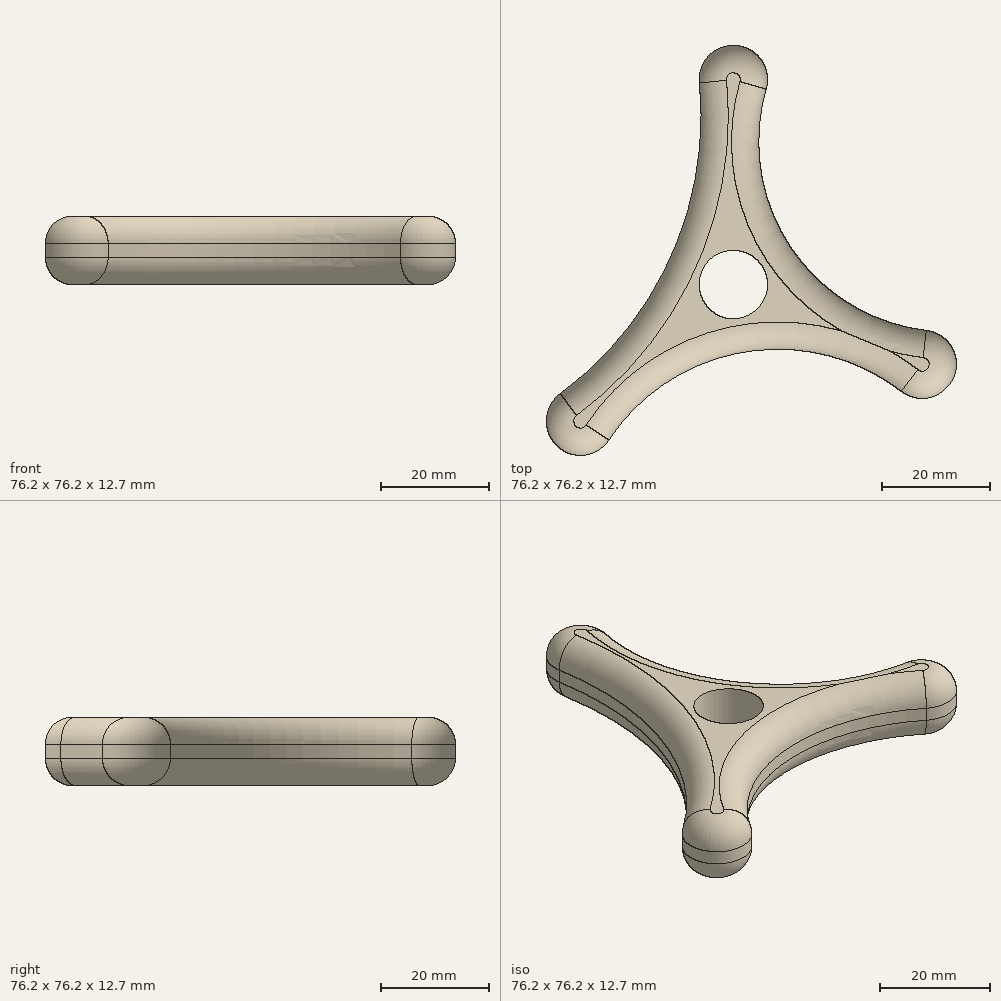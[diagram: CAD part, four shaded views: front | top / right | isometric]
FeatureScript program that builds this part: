
annotation { "Feature Type Name" : "Feature", "Feature Type Description" : "" }
export const myFeature = defineFeature(function(context is Context, id is Id, definition is map)
    precondition{}
    {
        {
            var Q0;
            Q0=qCreatedBy(makeId("Top.planeOp"),FACE);
            var sketch = newSketch(context, id + "F0", { "sketchPlane" : qUnion([Q0])});
            skCircle(sketch, "E0", {"center": v(0, 0) * mm, "radius": 6.35 * mm});
            skCircle(sketch, "E1", {"center": v(0, 0) * mm, "radius": 12.7 * mm});
            skCircle(sketch, "E2", {"center": v(0, 38.1) * mm, "radius": 6.35 * mm});
            skCircle(sketch, "E3", {"center": v(-28.4, -25.4) * mm, "radius": 6.35 * mm});
            skCircle(sketch, "E4", {"center": v(35.1, -14.81) * mm, "radius": 6.35 * mm});
            skArc(sketch, "E5", {"start": v(-32.15, -20.28) * mm, "mid": v(-11.6, 5.18) * mm, "end": v(-6.32, 37.49) * mm});
            skArc(sketch, "E6", {"start": v(31.22, -19.84) * mm, "mid": v(2.09, -12.53) * mm, "end": v(-23.1, -28.9) * mm});
            skArc(sketch, "E7", {"start": v(6.1, 36.33) * mm, "mid": v(10.58, 7.02) * mm, "end": v(35.84, -8.5) * mm});
            skSolve(sketch);
        }
        {
            var Q0;
            {var subQ0=sQuery(id+"F0.wireOp",EDGE,"E5");var subQ1=sQuery(id+"F0.wireOp",EDGE,"E1");var subQ2=makeQuery(id+"F0.imprint","INTERSECT",VERTEX,{"derivedFrom":[subQ1,subQ0]});Q0=makeQuery(id+"F0.imprint","IMPRINT",FACE,{"disambiguationData":[TD([[makeQuery(id+"F0.imprint","IMPRINT",EDGE,{"disambiguationData":[TD([[subQ2,-1.0]])],"derivedFrom":subQ1}),-1.0]])]});}
            var Q1;
            {var subQ0=sQuery(id+"F0.wireOp",EDGE,"E7");var subQ1=sQuery(id+"F0.wireOp",EDGE,"E1");var subQ2=makeQuery(id+"F0.imprint","INTERSECT",VERTEX,{"derivedFrom":[subQ1,subQ0]});Q1=makeQuery(id+"F0.imprint","IMPRINT",FACE,{"disambiguationData":[TD([[makeQuery(id+"F0.imprint","IMPRINT",EDGE,{"disambiguationData":[TD([[subQ2,1.0]])],"derivedFrom":subQ1}),-1.0]])]});}
            var Q2;
            {var subQ0=sQuery(id+"F0.wireOp",EDGE,"E5");var subQ1=sQuery(id+"F0.wireOp",EDGE,"E1");var subQ2=makeQuery(id+"F0.imprint","INTERSECT",VERTEX,{"derivedFrom":[subQ1,subQ0]});Q2=makeQuery(id+"F0.imprint","IMPRINT",FACE,{"disambiguationData":[TD([[makeQuery(id+"F0.imprint","IMPRINT",EDGE,{"disambiguationData":[TD([[subQ2,1.0]])],"derivedFrom":subQ1}),-1.0]])]});}
            var Q3;
            Q3=makeQuery(id+"F0.imprint","IMPRINT",FACE,{"disambiguationData":[TD([[makeQuery(id+"F0.imprint","IMPRINT",EDGE,{"derivedFrom":sQuery(id+"F0.wireOp",EDGE,"E0")}),-1.0]])]});
            var Q4;
            {var subQ0=sQuery(id+"F0.wireOp",EDGE,"E3");var subQ1=makeQuery(id+"F0.imprint","INTERSECT",VERTEX,{"derivedFrom":[subQ0,sQuery(id+"F0.wireOp",EDGE,"E5")]});Q4=makeQuery(id+"F0.imprint","IMPRINT",FACE,{"disambiguationData":[TD([[makeQuery(id+"F0.imprint","IMPRINT",EDGE,{"disambiguationData":[TD([[subQ1,-1.0]])],"derivedFrom":subQ0}),1.0]])]});}
            var Q5;
            {var subQ0=sQuery(id+"F0.wireOp",EDGE,"E4");var subQ1=makeQuery(id+"F0.imprint","INTERSECT",VERTEX,{"derivedFrom":[subQ0,sQuery(id+"F0.wireOp",EDGE,"E6")]});Q5=makeQuery(id+"F0.imprint","IMPRINT",FACE,{"disambiguationData":[TD([[makeQuery(id+"F0.imprint","IMPRINT",EDGE,{"disambiguationData":[TD([[subQ1,1.0]])],"derivedFrom":subQ0}),1.0]])]});}
            var Q6;
            {var subQ0=sQuery(id+"F0.wireOp",EDGE,"E2");var subQ1=makeQuery(id+"F0.imprint","INTERSECT",VERTEX,{"derivedFrom":[subQ0,sQuery(id+"F0.wireOp",EDGE,"E5")]});Q6=makeQuery(id+"F0.imprint","IMPRINT",FACE,{"disambiguationData":[TD([[makeQuery(id+"F0.imprint","IMPRINT",EDGE,{"disambiguationData":[TD([[subQ1,-1.0]])],"derivedFrom":subQ0}),1.0]])]});}
            extrude(context, id + "F1", {"entities" : qUnion([Q0, Q1, Q2, Q3, Q4, Q5, Q6]), "depth" : 12.7 * mm, "offsetDistance" : 25.4 * mm});
        }
        {
            var Q0;
            Q0=makeQuery(id+"F1.opExtrude","CAP_EDGE",EDGE,{"disambiguationData":[OSD([sQuery(id+"F0.wireOp",EDGE,"E7")])],"isStart":false});
            var Q1;
            Q1=makeQuery(id+"F1.opExtrude","CAP_EDGE",EDGE,{"disambiguationData":[OSD([sQuery(id+"F0.wireOp",EDGE,"E5")])],"isStart":false});
            var Q2;
            Q2=makeQuery(id+"F1.opExtrude","CAP_EDGE",EDGE,{"disambiguationData":[OSD([sQuery(id+"F0.wireOp",EDGE,"E2")])],"isStart":false});
            var Q3;
            Q3=makeQuery(id+"F1.opExtrude","CAP_EDGE",EDGE,{"disambiguationData":[OSD([sQuery(id+"F0.wireOp",EDGE,"E3")])],"isStart":false});
            var Q4;
            Q4=makeQuery(id+"F1.opExtrude","CAP_EDGE",EDGE,{"disambiguationData":[OSD([sQuery(id+"F0.wireOp",EDGE,"E6")])],"isStart":true});
            var Q5;
            Q5=makeQuery(id+"F1.opExtrude","CAP_EDGE",EDGE,{"disambiguationData":[OSD([sQuery(id+"F0.wireOp",EDGE,"E4")])],"isStart":true});
            var Q6;
            Q6=makeQuery(id+"F1.opExtrude","CAP_EDGE",EDGE,{"disambiguationData":[OSD([sQuery(id+"F0.wireOp",EDGE,"E6")])],"isStart":false});
            var Q7;
            Q7=makeQuery(id+"F1.opExtrude","CAP_EDGE",EDGE,{"disambiguationData":[OSD([sQuery(id+"F0.wireOp",EDGE,"E4")])],"isStart":false});
            var Q8;
            Q8=makeQuery(id+"F1.opExtrude","CAP_EDGE",EDGE,{"disambiguationData":[OSD([sQuery(id+"F0.wireOp",EDGE,"E3")])],"isStart":true});
            var Q9;
            Q9=makeQuery(id+"F1.opExtrude","CAP_EDGE",EDGE,{"disambiguationData":[OSD([sQuery(id+"F0.wireOp",EDGE,"E5")])],"isStart":true});
            var Q10;
            Q10=makeQuery(id+"F1.opExtrude","CAP_EDGE",EDGE,{"disambiguationData":[OSD([sQuery(id+"F0.wireOp",EDGE,"E2")])],"isStart":true});
            var Q11;
            Q11=makeQuery(id+"F1.opExtrude","CAP_EDGE",EDGE,{"disambiguationData":[OSD([sQuery(id+"F0.wireOp",EDGE,"E7")])],"isStart":true});
            fillet(context, id + "F2", {"entities" : qUnion([Q0, Q1, Q2, Q3, Q4, Q5, Q6, Q7, Q8, Q9, Q10, Q11]), "radius" : 5.08 * mm, "tangentPropagation" : true, "allowEdgeOverflow" : false});
        }
    });
